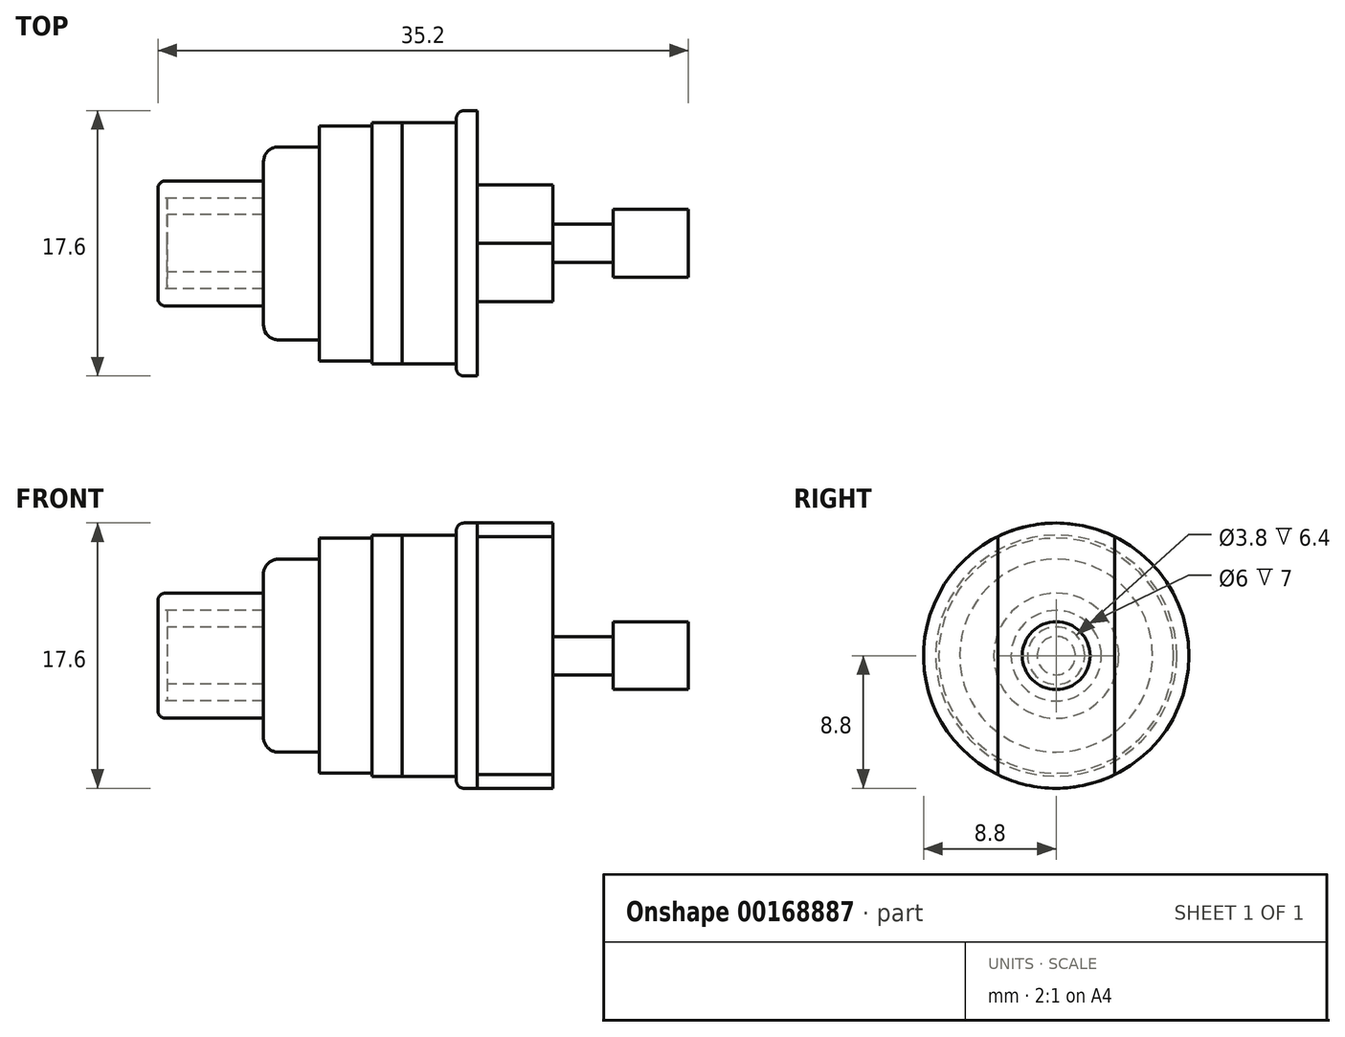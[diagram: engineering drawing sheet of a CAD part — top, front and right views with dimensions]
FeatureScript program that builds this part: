
annotation { "Feature Type Name" : "Feature", "Feature Type Description" : "" }
export const myFeature = defineFeature(function(context is Context, id is Id, definition is map)
    precondition{}
    {
        {
            var Q0;
            Q0=qCreatedBy(makeId("Front.planeOp"),FACE);
            var sketch = newSketch(context, id + "F0", { "sketchPlane" : qUnion([Q0])});
            skLineSegment(sketch, "E0", {"start": v(0, 7.8) * mm, "end": v(-3.5, 7.8) * mm});
            skLineSegment(sketch, "E1", {"start": v(-3.5, 7.8) * mm, "end": v(-3.5, 0) * mm});
            skLineSegment(sketch, "E2", {"start": v(-3.5, 0) * mm, "end": v(0, 0) * mm});
            skLineSegment(sketch, "E3", {"start": v(0, 0) * mm, "end": v(0, 7.8) * mm});
            skLineSegment(sketch, "E4", {"start": v(-3.5, 6.4) * mm, "end": v(-6.2, 6.4) * mm});
            skLineSegment(sketch, "E5", {"start": v(-7.2, 5.4) * mm, "end": v(-7.2, 0) * mm});
            skLineSegment(sketch, "E6", {"start": v(-7.2, 0) * mm, "end": v(-3.5, 0) * mm});
            skLineSegment(sketch, "E7", {"start": v(-7.2, 4.15) * mm, "end": v(-13.7, 4.15) * mm});
            skLineSegment(sketch, "E8", {"start": v(-14.2, 3.65) * mm, "end": v(-14.2, 3) * mm});
            skLineSegment(sketch, "E9", {"start": v(-14.2, 3) * mm, "end": v(-7.2, 3) * mm});
            skLineSegment(sketch, "E10", {"start": v(0, 7.8) * mm, "end": v(0, 8) * mm});
            skLineSegment(sketch, "E11", {"start": v(0, 8) * mm, "end": v(2, 8) * mm});
            skLineSegment(sketch, "E12", {"start": v(2, 8) * mm, "end": v(2, 0) * mm});
            skLineSegment(sketch, "E13", {"start": v(2, 0) * mm, "end": v(0, 0) * mm});
            skLineSegment(sketch, "E14", {"start": v(2, 8) * mm, "end": v(5.6, 8) * mm});
            skLineSegment(sketch, "E15", {"start": v(5.6, 8) * mm, "end": v(5.6, 8.3) * mm});
            skLineSegment(sketch, "E16", {"start": v(6.1, 8.8) * mm, "end": v(7, 8.8) * mm});
            skLineSegment(sketch, "E17", {"start": v(7, 8.8) * mm, "end": v(7, 0) * mm});
            skLineSegment(sketch, "E18", {"start": v(7, 0) * mm, "end": v(2, 0) * mm});
            skLineSegment(sketch, "E19", {"start": v(-13.18, 0) * mm, "end": v(10.16, 0) * mm, "construction": true});
            skPoint(sketch, "E19.endSnap0", {"position": v(1, 0) * mm});
            skPoint(sketch, "E20.visualSharp", {"position": v(5.6, 8.8) * mm});
            skArc(sketch, "E20.filletArc", {"start": v(6.1, 8.8) * mm, "mid": v(5.75, 8.65) * mm, "end": v(5.6, 8.3) * mm});
            skPoint(sketch, "E21.visualSharp", {"position": v(-7.2, 6.4) * mm});
            skArc(sketch, "E21.filletArc", {"start": v(-6.2, 6.4) * mm, "mid": v(-6.9, 6.1) * mm, "end": v(-7.2, 5.4) * mm});
            skPoint(sketch, "E22.visualSharp", {"position": v(-14.2, 4.15) * mm});
            skArc(sketch, "E22.filletArc", {"start": v(-13.7, 4.15) * mm, "mid": v(-14.05, 4) * mm, "end": v(-14.2, 3.65) * mm});
            skLineSegment(sketch, "E23", {"start": v(-13.6, 3) * mm, "end": v(-13.6, 1.9) * mm});
            skLineSegment(sketch, "E24", {"start": v(-13.6, 1.9) * mm, "end": v(-7.2, 1.9) * mm});
            skSolve(sketch);
        }
        {
            var Q0;
            {var subQ0=sQuery(id+"F0.wireOp",EDGE,"E7");Q0=makeQuery(id+"F0.imprint","IMPRINT",FACE,{"disambiguationData":[TD([[makeQuery(id+"F0.imprint","IMPRINT",EDGE,{"derivedFrom":subQ0}),1.0]])]});}
            var Q1;
            Q1=sQuery(id+"F0.wireOp",EDGE,"E19");
            revolve(context, id + "F1", {"entities" : qUnion([Q0]), "axis" : qUnion([Q1]), "revolveType" : RevolveType.FULL});
        }
        {
            var Q0;
            {var subQ3=sQuery(id+"F0.wireOp",EDGE,"E4");Q0=makeQuery(id+"F0.imprint","IMPRINT",FACE,{"disambiguationData":[TD([[makeQuery(id+"F0.imprint","IMPRINT",EDGE,{"derivedFrom":subQ3}),1.0]])]});}
            var Q1;
            Q1=sQuery(id+"F0.wireOp",EDGE,"E6");
            revolve(context, id + "F2", {"entities" : qUnion([Q0]), "axis" : qUnion([Q1]), "revolveType" : RevolveType.FULL});
        }
        {
            var Q0;
            {var subQ3=sQuery(id+"F0.wireOp",EDGE,"E0");Q0=makeQuery(id+"F0.imprint","IMPRINT",FACE,{"disambiguationData":[TD([[makeQuery(id+"F0.imprint","IMPRINT",EDGE,{"derivedFrom":subQ3}),1.0]])]});}
            var Q1;
            Q1=sQuery(id+"F0.wireOp",EDGE,"E2");
            revolve(context, id + "F3", {"entities" : qUnion([Q0]), "axis" : qUnion([Q1]), "revolveType" : RevolveType.FULL});
        }
        {
            var Q0;
            Q0=makeQuery(id+"F0.imprint","IMPRINT",FACE,{"disambiguationData":[TD([[makeQuery(id+"F0.imprint","IMPRINT",EDGE,{"derivedFrom":sQuery(id+"F0.wireOp",EDGE,"E3")}),-1.0]])]});
            var Q1;
            Q1=sQuery(id+"F0.wireOp",EDGE,"E18");
            revolve(context, id + "F4", {"entities" : qUnion([Q0]), "axis" : qUnion([Q1]), "revolveType" : RevolveType.FULL});
        }
        {
            var Q0;
            {var subQ4=sQuery(id+"F0.wireOp",EDGE,"E23");Q0=makeQuery(id+"F0.imprint","IMPRINT",FACE,{"disambiguationData":[TD([[makeQuery(id+"F0.imprint","IMPRINT",EDGE,{"derivedFrom":subQ4}),1.0]])]});}
            var Q1;
            Q1=sQuery(id+"F0.wireOp",EDGE,"E19");
            revolve(context, id + "F5", {"entities" : qUnion([Q0]), "axis" : qUnion([Q1]), "revolveType" : RevolveType.FULL});
        }
        {
            var Q0;
            Q0=makeQuery(id+"F0.imprint","IMPRINT",FACE,{"disambiguationData":[TD([[makeQuery(id+"F0.imprint","IMPRINT",EDGE,{"derivedFrom":sQuery(id+"F0.wireOp",EDGE,"E12")}),1.0]])]});
            var Q1;
            Q1=sQuery(id+"F0.wireOp",EDGE,"E19");
            revolve(context, id + "F6", {"entities" : qUnion([Q0]), "axis" : qUnion([Q1]), "revolveType" : RevolveType.FULL});
        }
        {
            var Q0;
            Q0=makeQuery(id+"F6.opRevolve","SWEPT_FACE",FACE,{"disambiguationData":[OSD([sQuery(id+"F0.wireOp",EDGE,"E17")])]});
            var sketch = newSketch(context, id + "F7", { "sketchPlane" : qUnion([Q0])});
            skLineSegment(sketch, "E25.left", {"start": v(-3.87, 7.9) * mm, "end": v(-3.87, -7.9) * mm});
            skLineSegment(sketch, "E25.right", {"start": v(3.87, 7.9) * mm, "end": v(3.87, -7.9) * mm});
            skArc(sketch, "E26", {"start": v(0, 8.8) * mm, "mid": v(-1.99, 8.57) * mm, "end": v(-3.87, 7.9) * mm});
            skArc(sketch, "E27", {"start": v(3.87, 7.9) * mm, "mid": v(1.99, 8.56) * mm, "end": v(0, 8.8) * mm});
            skArc(sketch, "E28", {"start": v(0, -8.8) * mm, "mid": v(1.99, -8.56) * mm, "end": v(3.87, -7.9) * mm});
            skArc(sketch, "E29", {"start": v(-3.87, -7.9) * mm, "mid": v(-1.99, -8.57) * mm, "end": v(0, -8.8) * mm});
            skSolve(sketch);
        }
        {
            var Q0;
            Q0 = qSketchRegion(id + "F7", true);
            extrude(context, id + "F8", {"entities" : qUnion([Q0]), "depth" : 5 * mm});
        }
        {
            var Q0;
            Q0=makeQuery(id+"F8.opExtrude","CAP_FACE",FACE,{"disambiguationData":[OSD([sQuery(id+"F7.wireOp",EDGE,"E25.left"),sQuery(id+"F7.wireOp",EDGE,"E25.right"),sQuery(id+"F7.wireOp",EDGE,"E26"),sQuery(id+"F7.wireOp",EDGE,"E27"),sQuery(id+"F7.wireOp",EDGE,"E28"),sQuery(id+"F7.wireOp",EDGE,"E29")])],"isStart":false});
            var sketch = newSketch(context, id + "F9", { "sketchPlane" : qUnion([Q0])});
            skCircle(sketch, "E30", {"center": v(0, 0) * mm, "radius": 1.27 * mm});
            skSolve(sketch);
        }
        {
            var Q0;
            Q0 = qSketchRegion(id + "F9", true);
            extrude(context, id + "F10", {"entities" : qUnion([Q0]), "operationType" : NewBodyOperationType.ADD, "depth" : 4 * mm});
        }
        {
            var Q0;
            Q0=makeQuery(id+"F10.opExtrude","CAP_FACE",FACE,{"disambiguationData":[OSD([sQuery(id+"F9.wireOp",EDGE,"E30")])],"isStart":false});
            var sketch = newSketch(context, id + "F11", { "sketchPlane" : qUnion([Q0])});
            skCircle(sketch, "E31", {"center": v(0, 0) * mm, "radius": 2.25 * mm});
            skSolve(sketch);
        }
        {
            var Q0;
            Q0 = qSketchRegion(id + "F11", true);
            extrude(context, id + "F12", {"entities" : qUnion([Q0]), "operationType" : NewBodyOperationType.ADD, "depth" : 5 * mm});
        }
    });
